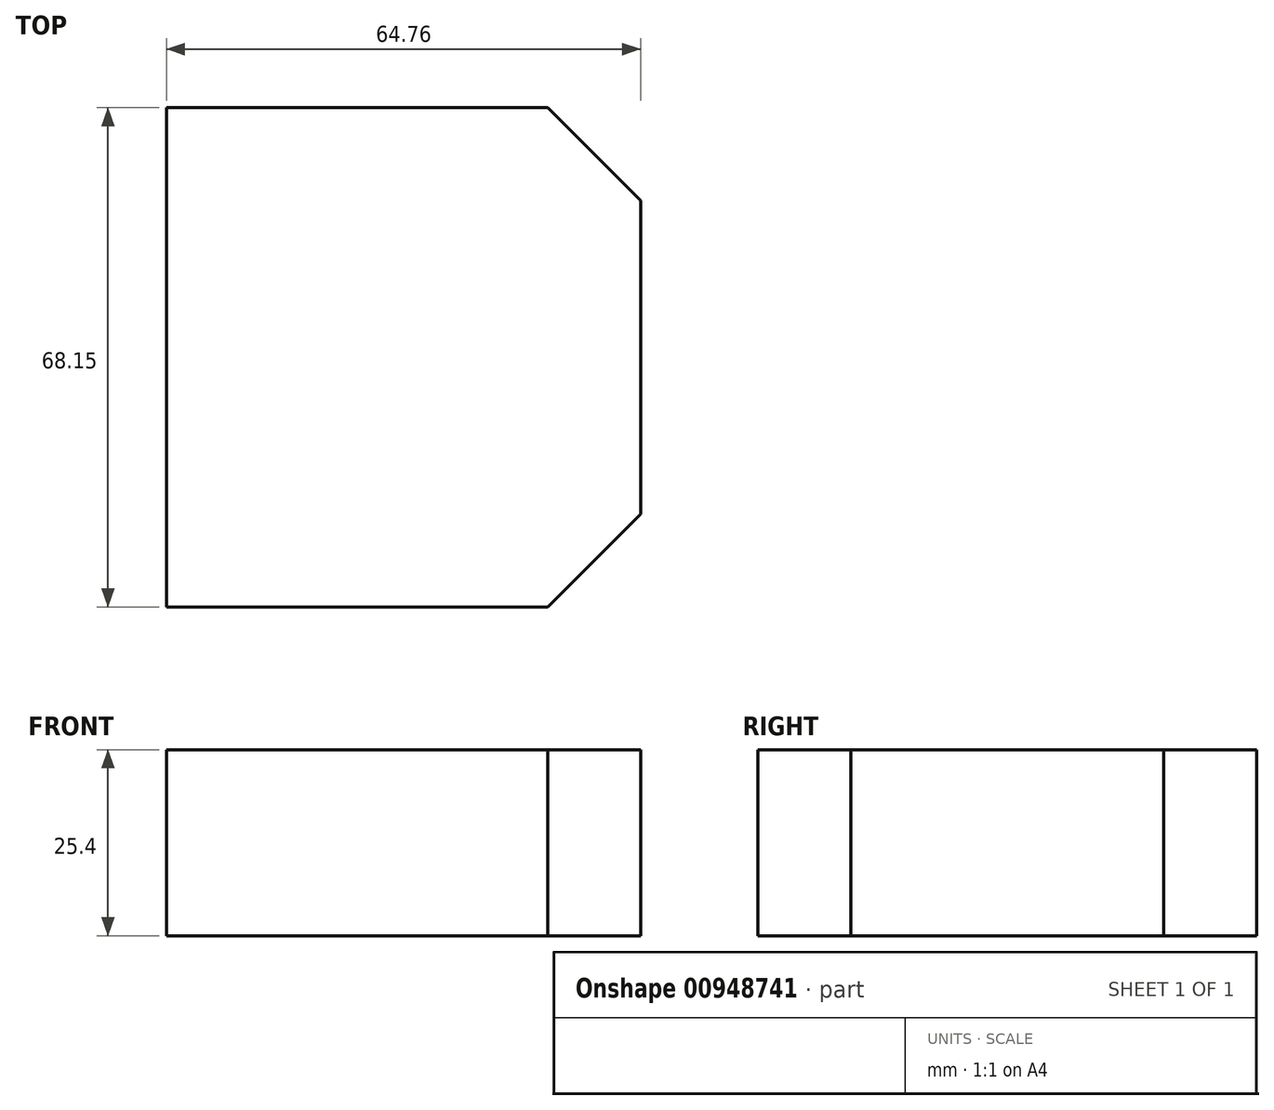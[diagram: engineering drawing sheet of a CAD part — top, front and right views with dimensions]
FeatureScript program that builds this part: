
annotation { "Feature Type Name" : "Feature", "Feature Type Description" : "" }
export const myFeature = defineFeature(function(context is Context, id is Id, definition is map)
    precondition{}
    {
        {
            var Q0;
            Q0=qCreatedBy(makeId("Top.planeOp"),FACE);
            var sketch = newSketch(context, id + "F0", { "sketchPlane" : qUnion([Q0])});
            skLineSegment(sketch, "E0.bottom", {"start": v(0, 0) * mm, "end": v(64.76, 0) * mm});
            skLineSegment(sketch, "E0.top", {"start": v(0, 68.15) * mm, "end": v(64.76, 68.15) * mm});
            skLineSegment(sketch, "E0.left", {"start": v(0, 0) * mm, "end": v(0, 68.15) * mm});
            skLineSegment(sketch, "E0.right", {"start": v(64.76, 0) * mm, "end": v(64.76, 68.15) * mm});
            skSolve(sketch);
        }
        {
            var Q0;
            Q0=makeQuery(id+"F0.imprint","IMPRINT",FACE,{"disambiguationData":[TD([[makeQuery(id+"F0.imprint","IMPRINT",EDGE,{"derivedFrom":sQuery(id+"F0.wireOp",EDGE,"E0.bottom")}),1.0]])]});
            extrude(context, id + "F1", {"entities" : qUnion([Q0]), "depth" : 25.4 * mm, "offsetDistance" : 25.4 * mm});
        }
        {
            var Q0;
            Q0=makeQuery(id+"F1.opExtrude","SWEPT_EDGE",EDGE,{"disambiguationData":[OSD([sQuery(id+"F0.wireOp",EDGE,"E0.bottom"),sQuery(id+"F0.wireOp",EDGE,"E0.right")])]});
            var Q1;
            Q1=makeQuery(id+"F1.opExtrude","SWEPT_EDGE",EDGE,{"disambiguationData":[OSD([sQuery(id+"F0.wireOp",EDGE,"E0.top"),sQuery(id+"F0.wireOp",EDGE,"E0.right")])]});
            chamfer(context, id + "F2", {"entities" : qUnion([Q0, Q1]), "width" : 12.7 * mm, "tangentPropagation" : true});
        }
    });
